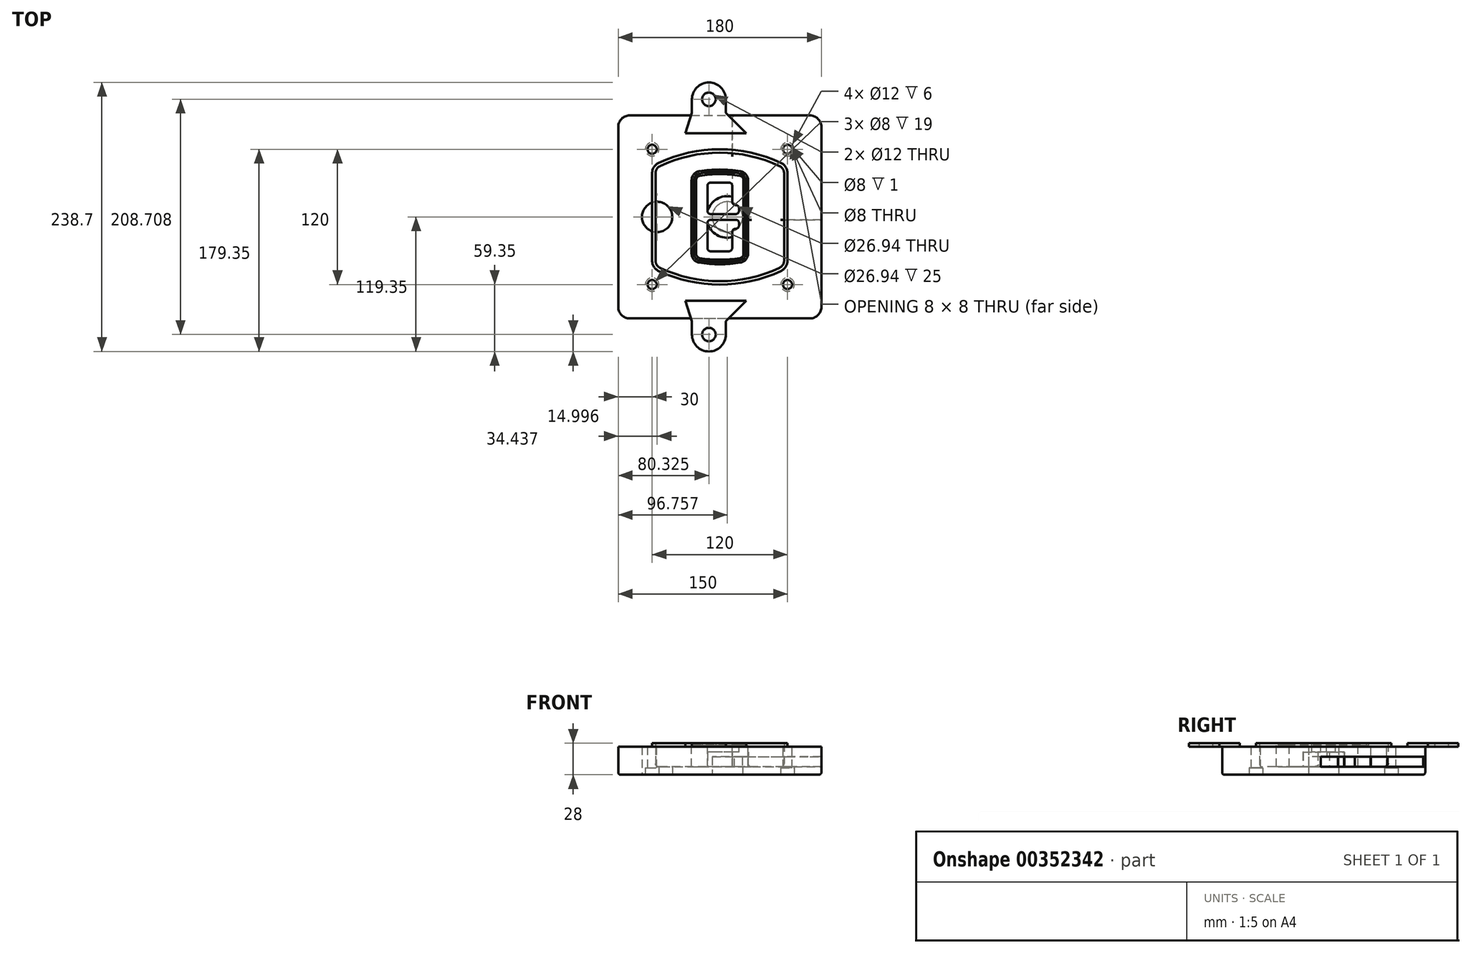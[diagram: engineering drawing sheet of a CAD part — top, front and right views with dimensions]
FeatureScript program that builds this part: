
annotation { "Feature Type Name" : "Feature", "Feature Type Description" : "" }
export const myFeature = defineFeature(function(context is Context, id is Id, definition is map)
    precondition{}
    {
        {
            var Q0;
            Q0=qCreatedBy(makeId("Top.planeOp"),FACE);
            var sketch = newSketch(context, id + "F0", { "sketchPlane" : qUnion([Q0])});
            skPoint(sketch, "E0.rect.middle", {"position": v(0, 0) * mm});
            skLineSegment(sketch, "E1.bottom", {"start": v(-80, -90) * mm, "end": v(80, -90) * mm});
            skLineSegment(sketch, "E1.top", {"start": v(-80, 90) * mm, "end": v(80, 90) * mm});
            skLineSegment(sketch, "E1.left", {"start": v(-90, -80) * mm, "end": v(-90, 80) * mm});
            skLineSegment(sketch, "E1.right", {"start": v(90, -80) * mm, "end": v(90, 80) * mm});
            skLineSegment(sketch, "E2", {"start": v(-90, 90) * mm, "end": v(90, -90) * mm, "construction": true});
            skLineSegment(sketch, "E3", {"start": v(90, 90) * mm, "end": v(-90, -90) * mm, "construction": true});
            skCircle(sketch, "E4", {"center": v(-60, 60) * mm, "radius": 4 * mm});
            skCircle(sketch, "E5", {"center": v(60, 60) * mm, "radius": 4 * mm});
            skCircle(sketch, "E6", {"center": v(60, -60) * mm, "radius": 4 * mm});
            skCircle(sketch, "E7", {"center": v(-60, -60) * mm, "radius": 4 * mm});
            skLineSegment(sketch, "E8", {"start": v(-60, 60) * mm, "end": v(60, 60) * mm, "construction": true});
            skLineSegment(sketch, "E9", {"start": v(60, 60) * mm, "end": v(60, -60) * mm, "construction": true});
            skLineSegment(sketch, "E10", {"start": v(60, -60) * mm, "end": v(-60, -60) * mm, "construction": true});
            skLineSegment(sketch, "E11", {"start": v(-60, -60) * mm, "end": v(-60, 60) * mm, "construction": true});
            skLineSegment(sketch, "E12", {"start": v(-60, 38.83) * mm, "end": v(-60, -38.83) * mm});
            skLineSegment(sketch, "E13", {"start": v(60, 38.83) * mm, "end": v(60, -38.83) * mm});
            skArc(sketch, "E14", {"start": v(54.26, 47.88) * mm, "mid": v(0, 60) * mm, "end": v(-54.26, 47.88) * mm});
            skArc(sketch, "E15", {"start": v(-54.26, -47.88) * mm, "mid": v(0, -60) * mm, "end": v(54.26, -47.88) * mm});
            skLineSegment(sketch, "E16", {"start": v(-60, 0) * mm, "end": v(60, 0) * mm, "construction": true});
            skPoint(sketch, "E17.visualSharp", {"position": v(-60, -45) * mm});
            skArc(sketch, "E17.filletArc", {"start": v(-60, -38.83) * mm, "mid": v(-58.44, -44.2) * mm, "end": v(-54.26, -47.88) * mm});
            skPoint(sketch, "E18.visualSharp", {"position": v(-60, 45) * mm});
            skArc(sketch, "E18.filletArc", {"start": v(-54.26, 47.88) * mm, "mid": v(-58.44, 44.2) * mm, "end": v(-60, 38.83) * mm});
            skPoint(sketch, "E19.visualSharp", {"position": v(60, 45) * mm});
            skArc(sketch, "E19.filletArc", {"start": v(60, 38.83) * mm, "mid": v(58.44, 44.2) * mm, "end": v(54.26, 47.88) * mm});
            skPoint(sketch, "E20.visualSharp", {"position": v(60, -45) * mm});
            skArc(sketch, "E20.filletArc", {"start": v(54.26, -47.88) * mm, "mid": v(58.44, -44.2) * mm, "end": v(60, -38.83) * mm});
            skPoint(sketch, "E21.visualSharp", {"position": v(-90, 90) * mm});
            skArc(sketch, "E21.filletArc", {"start": v(-80, 90) * mm, "mid": v(-87.07, 87.07) * mm, "end": v(-90, 80) * mm});
            skPoint(sketch, "E22.visualSharp", {"position": v(90, 90) * mm});
            skArc(sketch, "E22.filletArc", {"start": v(90, 80) * mm, "mid": v(87.07, 87.07) * mm, "end": v(80, 90) * mm});
            skPoint(sketch, "E23.visualSharp", {"position": v(90, -90) * mm});
            skArc(sketch, "E23.filletArc", {"start": v(80, -90) * mm, "mid": v(87.07, -87.07) * mm, "end": v(90, -80) * mm});
            skPoint(sketch, "E24.visualSharp", {"position": v(-90, -90) * mm});
            skArc(sketch, "E24.filletArc", {"start": v(-90, -80) * mm, "mid": v(-87.07, -87.07) * mm, "end": v(-80, -90) * mm});
            skArc(sketch, "E25.0", {"start": v(57, 38.83) * mm, "mid": v(55.9, 42.58) * mm, "end": v(52.98, 45.17) * mm});
            skLineSegment(sketch, "E25.1", {"start": v(57, 38.83) * mm, "end": v(57, -38.83) * mm});
            skArc(sketch, "E25.2", {"start": v(52.98, -45.17) * mm, "mid": v(55.9, -42.58) * mm, "end": v(57, -38.83) * mm});
            skArc(sketch, "E25.3", {"start": v(-52.98, -45.17) * mm, "mid": v(0, -57) * mm, "end": v(52.98, -45.17) * mm});
            skArc(sketch, "E25.4", {"start": v(-57, -38.83) * mm, "mid": v(-55.9, -42.58) * mm, "end": v(-52.98, -45.17) * mm});
            skArc(sketch, "E25.5", {"start": v(52.98, 45.17) * mm, "mid": v(0, 57) * mm, "end": v(-52.98, 45.17) * mm});
            skLineSegment(sketch, "E25.6", {"start": v(-57, 38.83) * mm, "end": v(-57, -38.83) * mm});
            skArc(sketch, "E25.7", {"start": v(-52.98, 45.17) * mm, "mid": v(-55.9, 42.58) * mm, "end": v(-57, 38.83) * mm});
            skArc(sketch, "E26.0", {"start": v(-55.96, 51.5) * mm, "mid": v(-61.82, 46.33) * mm, "end": v(-64, 38.83) * mm});
            skArc(sketch, "E26.1", {"start": v(55.96, 51.5) * mm, "mid": v(0, 64) * mm, "end": v(-55.96, 51.5) * mm});
            skArc(sketch, "E26.2", {"start": v(64, 38.83) * mm, "mid": v(61.82, 46.33) * mm, "end": v(55.96, 51.5) * mm});
            skLineSegment(sketch, "E26.3", {"start": v(64, 38.83) * mm, "end": v(64, -38.83) * mm});
            skArc(sketch, "E26.4", {"start": v(55.96, -51.5) * mm, "mid": v(61.82, -46.33) * mm, "end": v(64, -38.83) * mm});
            skLineSegment(sketch, "E26.5", {"start": v(-64, 38.83) * mm, "end": v(-64, -38.83) * mm});
            skArc(sketch, "E26.6", {"start": v(-55.96, -51.5) * mm, "mid": v(0, -64) * mm, "end": v(55.96, -51.5) * mm});
            skArc(sketch, "E26.7", {"start": v(-64, -38.83) * mm, "mid": v(-61.82, -46.33) * mm, "end": v(-55.96, -51.5) * mm});
            skSolve(sketch);
        }
        {
            var Q0;
            Q0=makeQuery(id+"F0.imprint","IMPRINT",FACE,{"disambiguationData":[TD([[makeQuery(id+"F0.imprint","IMPRINT",EDGE,{"derivedFrom":sQuery(id+"F0.wireOp",EDGE,"E1.bottom")}),1.0]])]});
            var Q1;
            Q1=makeQuery(id+"F0.imprint","IMPRINT",FACE,{"disambiguationData":[TD([[makeQuery(id+"F0.imprint","IMPRINT",EDGE,{"derivedFrom":sQuery(id+"F0.wireOp",EDGE,"E12")}),1.0]])]});
            var Q2;
            Q2=makeQuery(id+"F0.imprint","IMPRINT",FACE,{"disambiguationData":[TD([[makeQuery(id+"F0.imprint","IMPRINT",EDGE,{"derivedFrom":sQuery(id+"F0.wireOp",EDGE,"E25.0")}),1.0]])]});
            var Q3;
            Q3=makeQuery(id+"F0.imprint","IMPRINT",FACE,{"disambiguationData":[TD([[makeQuery(id+"F0.imprint","IMPRINT",EDGE,{"derivedFrom":sQuery(id+"F0.wireOp",EDGE,"E12")}),-1.0]])]});
            extrude(context, id + "F1", {"entities" : qUnion([Q0, Q1, Q2, Q3]), "oppositeDirection" : true, "depth" : 25 * mm});
        }
        {
            var Q0;
            Q0=makeQuery(id+"F0.imprint","IMPRINT",FACE,{"disambiguationData":[TD([[makeQuery(id+"F0.imprint","IMPRINT",EDGE,{"derivedFrom":sQuery(id+"F0.wireOp",EDGE,"E12")}),1.0]])]});
            extrude(context, id + "F2", {"entities" : qUnion([Q0]), "operationType" : NewBodyOperationType.ADD, "depth" : 3 * mm});
        }
        {
            var Q0;
            Q0=makeQuery(id+"F0.imprint","IMPRINT",FACE,{"disambiguationData":[TD([[makeQuery(id+"F0.imprint","IMPRINT",EDGE,{"derivedFrom":sQuery(id+"F0.wireOp",EDGE,"E25.0")}),1.0]])]});
            extrude(context, id + "F3", {"entities" : qUnion([Q0]), "operationType" : NewBodyOperationType.REMOVE, "oppositeDirection" : true, "depth" : 18 * mm});
        }
        {
            var Q0;
            Q0=makeQuery(id+"F2.opExtrude","CAP_FACE",FACE,{"disambiguationData":[OSD([sQuery(id+"F0.wireOp",EDGE,"E12"),sQuery(id+"F0.wireOp",EDGE,"E13"),sQuery(id+"F0.wireOp",EDGE,"E14"),sQuery(id+"F0.wireOp",EDGE,"E15"),sQuery(id+"F0.wireOp",EDGE,"E17.filletArc"),sQuery(id+"F0.wireOp",EDGE,"E18.filletArc"),sQuery(id+"F0.wireOp",EDGE,"E19.filletArc"),sQuery(id+"F0.wireOp",EDGE,"E20.filletArc"),sQuery(id+"F0.wireOp",EDGE,"E25.0"),sQuery(id+"F0.wireOp",EDGE,"E25.1"),sQuery(id+"F0.wireOp",EDGE,"E25.2"),sQuery(id+"F0.wireOp",EDGE,"E25.3"),sQuery(id+"F0.wireOp",EDGE,"E25.4"),sQuery(id+"F0.wireOp",EDGE,"E25.5"),sQuery(id+"F0.wireOp",EDGE,"E25.6"),sQuery(id+"F0.wireOp",EDGE,"E25.7")])],"isStart":false});
            var sketch = newSketch(context, id + "F4", { "sketchPlane" : qUnion([Q0])});
            skArc(sketch, "E27.0", {"start": v(-18.34, -40.45) * mm, "mid": v(0, -42) * mm, "end": v(18.34, -40.45) * mm});
            skArc(sketch, "E28.0", {"start": v(18.34, 40.45) * mm, "mid": v(0, 42) * mm, "end": v(-18.34, 40.45) * mm});
            skLineSegment(sketch, "E29", {"start": v(-25, 32.57) * mm, "end": v(-25, -32.57) * mm});
            skLineSegment(sketch, "E30", {"start": v(25, 32.57) * mm, "end": v(25, -32.57) * mm});
            skLineSegment(sketch, "E31", {"start": v(-25, 39.1) * mm, "end": v(25, 39.1) * mm, "construction": true});
            skLineSegment(sketch, "E32", {"start": v(-25, -39.1) * mm, "end": v(25, -39.1) * mm, "construction": true});
            skPoint(sketch, "E33.visualSharp", {"position": v(-25, 39.1) * mm});
            skArc(sketch, "E33.filletArc", {"start": v(-18.34, 40.45) * mm, "mid": v(-23.11, 37.73) * mm, "end": v(-25, 32.57) * mm});
            skPoint(sketch, "E34.visualSharp", {"position": v(25, 39.1) * mm});
            skArc(sketch, "E34.filletArc", {"start": v(25, 32.57) * mm, "mid": v(23.11, 37.73) * mm, "end": v(18.34, 40.45) * mm});
            skPoint(sketch, "E35.visualSharp", {"position": v(25, -39.1) * mm});
            skArc(sketch, "E35.filletArc", {"start": v(18.34, -40.45) * mm, "mid": v(23.11, -37.73) * mm, "end": v(25, -32.57) * mm});
            skPoint(sketch, "E36.visualSharp", {"position": v(-25, -39.1) * mm});
            skArc(sketch, "E36.filletArc", {"start": v(-25, -32.57) * mm, "mid": v(-23.11, -37.73) * mm, "end": v(-18.34, -40.45) * mm});
            skArc(sketch, "E37.0", {"start": v(52.98, 45.17) * mm, "mid": v(0, 57) * mm, "end": v(-52.98, 45.17) * mm});
            skArc(sketch, "E37.1", {"start": v(-52.98, 45.17) * mm, "mid": v(-55.9, 42.58) * mm, "end": v(-57, 38.83) * mm});
            skLineSegment(sketch, "E37.2", {"start": v(-57, 38.83) * mm, "end": v(-57, -38.83) * mm});
            skArc(sketch, "E37.3", {"start": v(-57, -38.83) * mm, "mid": v(-55.9, -42.58) * mm, "end": v(-52.98, -45.17) * mm});
            skArc(sketch, "E37.4", {"start": v(-52.98, -45.17) * mm, "mid": v(0, -57) * mm, "end": v(52.98, -45.17) * mm});
            skArc(sketch, "E37.5", {"start": v(52.98, -45.17) * mm, "mid": v(55.9, -42.58) * mm, "end": v(57, -38.83) * mm});
            skLineSegment(sketch, "E37.6", {"start": v(57, 38.83) * mm, "end": v(57, -38.83) * mm});
            skArc(sketch, "E37.7", {"start": v(57, 38.83) * mm, "mid": v(55.9, 42.58) * mm, "end": v(52.98, 45.17) * mm});
            skLineSegment(sketch, "E38.0", {"start": v(23, 32.57) * mm, "end": v(23, -32.57) * mm});
            skArc(sketch, "E38.1", {"start": v(18, -38.48) * mm, "mid": v(21.58, -36.44) * mm, "end": v(23, -32.57) * mm});
            skArc(sketch, "E38.2", {"start": v(-18, -38.48) * mm, "mid": v(0, -40) * mm, "end": v(18, -38.48) * mm});
            skArc(sketch, "E38.3", {"start": v(-23, -32.57) * mm, "mid": v(-21.58, -36.44) * mm, "end": v(-18, -38.48) * mm});
            skLineSegment(sketch, "E38.4", {"start": v(-23, 32.57) * mm, "end": v(-23, -32.57) * mm});
            skArc(sketch, "E38.5", {"start": v(23, 32.57) * mm, "mid": v(21.58, 36.44) * mm, "end": v(18, 38.48) * mm});
            skArc(sketch, "E38.6", {"start": v(-18, 38.48) * mm, "mid": v(-21.58, 36.44) * mm, "end": v(-23, 32.57) * mm});
            skArc(sketch, "E38.7", {"start": v(18, 38.48) * mm, "mid": v(0, 40) * mm, "end": v(-18, 38.48) * mm});
            skArc(sketch, "E39.0", {"start": v(21, 32.57) * mm, "mid": v(20.06, 35.15) * mm, "end": v(17.67, 36.5) * mm});
            skLineSegment(sketch, "E39.1", {"start": v(21, 32.57) * mm, "end": v(21, -32.57) * mm});
            skArc(sketch, "E39.2", {"start": v(17.67, -36.5) * mm, "mid": v(20.06, -35.15) * mm, "end": v(21, -32.57) * mm});
            skArc(sketch, "E39.3", {"start": v(-17.67, -36.5) * mm, "mid": v(0, -38) * mm, "end": v(17.67, -36.5) * mm});
            skArc(sketch, "E39.4", {"start": v(-21, -32.57) * mm, "mid": v(-20.06, -35.15) * mm, "end": v(-17.67, -36.5) * mm});
            skArc(sketch, "E39.5", {"start": v(17.67, 36.5) * mm, "mid": v(0, 38) * mm, "end": v(-17.67, 36.5) * mm});
            skLineSegment(sketch, "E39.6", {"start": v(-21, 32.57) * mm, "end": v(-21, -32.57) * mm});
            skArc(sketch, "E39.7", {"start": v(-17.67, 36.5) * mm, "mid": v(-20.06, 35.15) * mm, "end": v(-21, 32.57) * mm});
            skLineSegment(sketch, "E40", {"start": v(-25, 0) * mm, "end": v(25, 0) * mm, "construction": true});
            skLineSegment(sketch, "E41", {"start": v(-11, 5.5) * mm, "end": v(-11, 27.5) * mm});
            skLineSegment(sketch, "E42", {"start": v(-8, 30.5) * mm, "end": v(8, 30.5) * mm});
            skLineSegment(sketch, "E43", {"start": v(11, 27.5) * mm, "end": v(11, 13.5) * mm});
            skLineSegment(sketch, "E44", {"start": v(14, 10.5) * mm, "end": v(14, 10.5) * mm});
            skLineSegment(sketch, "E45", {"start": v(17, 7.5) * mm, "end": v(17, 5.5) * mm});
            skLineSegment(sketch, "E46", {"start": v(14, 2.5) * mm, "end": v(-8, 2.5) * mm});
            skPoint(sketch, "E47.visualSharp", {"position": v(-11, 30.5) * mm});
            skArc(sketch, "E47.filletArc", {"start": v(-8, 30.5) * mm, "mid": v(-10.12, 29.62) * mm, "end": v(-11, 27.5) * mm});
            skPoint(sketch, "E48.visualSharp", {"position": v(11, 30.5) * mm});
            skArc(sketch, "E48.filletArc", {"start": v(11, 27.5) * mm, "mid": v(10.12, 29.62) * mm, "end": v(8, 30.5) * mm});
            skPoint(sketch, "E49.visualSharp", {"position": v(11, 10.5) * mm});
            skArc(sketch, "E49.filletArc", {"start": v(11, 13.5) * mm, "mid": v(11.88, 11.38) * mm, "end": v(14, 10.5) * mm});
            skPoint(sketch, "E50.visualSharp", {"position": v(17, 10.5) * mm});
            skArc(sketch, "E50.filletArc", {"start": v(17, 7.5) * mm, "mid": v(16.12, 9.62) * mm, "end": v(14, 10.5) * mm});
            skPoint(sketch, "E51.visualSharp", {"position": v(17, 2.5) * mm});
            skArc(sketch, "E51.filletArc", {"start": v(14, 2.5) * mm, "mid": v(16.12, 3.38) * mm, "end": v(17, 5.5) * mm});
            skPoint(sketch, "E52.visualSharp", {"position": v(-11, 2.5) * mm});
            skArc(sketch, "E52.filletArc", {"start": v(-11, 5.5) * mm, "mid": v(-10.12, 3.38) * mm, "end": v(-8, 2.5) * mm});
            skLineSegment(sketch, "E53.0.MirrorCS", {"start": v(14, -2.5) * mm, "end": v(-8, -2.5) * mm});
            skArc(sketch, "E54.0.MirrorCS", {"start": v(-11, -5.5) * mm, "mid": v(-10.12, -3.38) * mm, "end": v(-8, -2.5) * mm});
            skLineSegment(sketch, "E55.0.MirrorCS", {"start": v(-11, -5.5) * mm, "end": v(-11, -27.5) * mm});
            skArc(sketch, "E56.0.MirrorCS", {"start": v(-8, -30.5) * mm, "mid": v(-10.12, -29.62) * mm, "end": v(-11, -27.5) * mm});
            skLineSegment(sketch, "E57.0.MirrorCS", {"start": v(-8, -30.5) * mm, "end": v(8, -30.5) * mm});
            skArc(sketch, "E58.0.MirrorCS", {"start": v(11, -27.5) * mm, "mid": v(10.12, -29.62) * mm, "end": v(8, -30.5) * mm});
            skLineSegment(sketch, "E59.0.MirrorCS", {"start": v(11, -27.5) * mm, "end": v(11, -13.5) * mm});
            skArc(sketch, "E60.0.MirrorCS", {"start": v(11, -13.5) * mm, "mid": v(11.88, -11.38) * mm, "end": v(14, -10.5) * mm});
            skArc(sketch, "E61.0.MirrorCS", {"start": v(17, -7.5) * mm, "mid": v(16.12, -9.62) * mm, "end": v(14, -10.5) * mm});
            skLineSegment(sketch, "E62.0.MirrorCS", {"start": v(17, -7.5) * mm, "end": v(17, -5.5) * mm});
            skArc(sketch, "E63.0.MirrorCS", {"start": v(14, -2.5) * mm, "mid": v(16.12, -3.38) * mm, "end": v(17, -5.5) * mm});
            skSolve(sketch);
        }
        {
            var Q0;
            Q0=makeQuery(id+"F4.imprint","IMPRINT",FACE,{"disambiguationData":[TD([[makeQuery(id+"F4.imprint","IMPRINT",EDGE,{"derivedFrom":sQuery(id+"F4.wireOp",EDGE,"E27.0")}),1.0]])]});
            var Q1;
            Q1=makeQuery(id+"F4.imprint","IMPRINT",FACE,{"disambiguationData":[TD([[makeQuery(id+"F4.imprint","IMPRINT",EDGE,{"derivedFrom":sQuery(id+"F4.wireOp",EDGE,"E38.0")}),-1.0]])]});
            var Q2;
            Q2=makeQuery(id+"F4.imprint","IMPRINT",FACE,{"disambiguationData":[TD([[makeQuery(id+"F4.imprint","IMPRINT",EDGE,{"derivedFrom":sQuery(id+"F4.wireOp",EDGE,"E39.0")}),1.0]])]});
            extrude(context, id + "F5", {"entities" : qUnion([Q0, Q1, Q2]), "operationType" : NewBodyOperationType.ADD, "endBound" : BoundingType.UP_TO_NEXT, "oppositeDirection" : true, "depth" : 25 * mm});
        }
        {
            var Q0;
            Q0=makeQuery(id+"F4.imprint","IMPRINT",FACE,{"disambiguationData":[TD([[makeQuery(id+"F4.imprint","IMPRINT",EDGE,{"derivedFrom":sQuery(id+"F4.wireOp",EDGE,"E38.0")}),-1.0]])]});
            extrude(context, id + "F6", {"entities" : qUnion([Q0]), "operationType" : NewBodyOperationType.REMOVE, "oppositeDirection" : true, "depth" : 2 * mm});
        }
        {
            var Q0;
            Q0=makeQuery(id+"F1.opExtrude","CAP_FACE",FACE,{"disambiguationData":[OSD([sQuery(id+"F0.wireOp",EDGE,"E1.bottom"),sQuery(id+"F0.wireOp",EDGE,"E1.top"),sQuery(id+"F0.wireOp",EDGE,"E1.left"),sQuery(id+"F0.wireOp",EDGE,"E1.right"),sQuery(id+"F0.wireOp",EDGE,"E4"),sQuery(id+"F0.wireOp",EDGE,"E5"),sQuery(id+"F0.wireOp",EDGE,"E6"),sQuery(id+"F0.wireOp",EDGE,"E7"),sQuery(id+"F0.wireOp",EDGE,"E21.filletArc"),sQuery(id+"F0.wireOp",EDGE,"E22.filletArc"),sQuery(id+"F0.wireOp",EDGE,"E23.filletArc"),sQuery(id+"F0.wireOp",EDGE,"E24.filletArc")])],"isStart":false});
            var sketch = newSketch(context, id + "F7", { "sketchPlane" : qUnion([Q0])});
            skCircle(sketch, "E64", {"center": v(6.76, 0) * mm, "radius": 13.47 * mm});
            skCircle(sketch, "E65", {"center": v(-55.56, 0) * mm, "radius": 13.47 * mm});
            skLineSegment(sketch, "E66", {"start": v(90, 0) * mm, "end": v(-90, 0) * mm});
            skCircle(sketch, "E67", {"center": v(6.76, 0) * mm, "radius": 18.47 * mm});
            skCircle(sketch, "E68", {"center": v(60, -60) * mm, "radius": 6 * mm});
            skCircle(sketch, "E69", {"center": v(-60, -60) * mm, "radius": 6 * mm});
            skCircle(sketch, "E70", {"center": v(-60, 60) * mm, "radius": 6 * mm});
            skCircle(sketch, "E71", {"center": v(60, 60) * mm, "radius": 6 * mm});
            skSolve(sketch);
        }
        {
            var Q0;
            {var subQ1=sQuery(id+"F7.wireOp",EDGE,"E66");var subQ4=sQuery(id+"F7.wireOp",EDGE,"E64");var subQ6=makeQuery(id+"F7.imprint","INTERSECT",VERTEX,{"disambiguationData":[OD(0.0)],"derivedFrom":[subQ4,subQ1]});Q0=makeQuery(id+"F7.imprint","IMPRINT",FACE,{"disambiguationData":[TD([[makeQuery(id+"F7.imprint","IMPRINT",EDGE,{"disambiguationData":[TD([[subQ6,-1.0]])],"derivedFrom":subQ4}),-1.0]])]});}
            var Q1;
            {var subQ0=sQuery(id+"F7.wireOp",EDGE,"E66");var subQ1=sQuery(id+"F7.wireOp",EDGE,"E64");var subQ3=makeQuery(id+"F7.imprint","INTERSECT",VERTEX,{"disambiguationData":[OD(0.0)],"derivedFrom":[subQ1,subQ0]});Q1=makeQuery(id+"F7.imprint","IMPRINT",FACE,{"disambiguationData":[TD([[makeQuery(id+"F7.imprint","IMPRINT",EDGE,{"disambiguationData":[TD([[subQ3,-1.0]])],"derivedFrom":subQ1}),1.0]])]});}
            var Q2;
            {var subQ0=sQuery(id+"F7.wireOp",EDGE,"E66");var subQ1=sQuery(id+"F7.wireOp",EDGE,"E64");var subQ3=makeQuery(id+"F7.imprint","INTERSECT",VERTEX,{"disambiguationData":[OD(0.0)],"derivedFrom":[subQ1,subQ0]});Q2=makeQuery(id+"F7.imprint","IMPRINT",FACE,{"disambiguationData":[TD([[makeQuery(id+"F7.imprint","IMPRINT",EDGE,{"disambiguationData":[TD([[subQ3,1.0]])],"derivedFrom":subQ1}),1.0]])]});}
            var Q3;
            {var subQ1=sQuery(id+"F7.wireOp",EDGE,"E66");var subQ4=sQuery(id+"F7.wireOp",EDGE,"E64");var subQ6=makeQuery(id+"F7.imprint","INTERSECT",VERTEX,{"disambiguationData":[OD(0.0)],"derivedFrom":[subQ4,subQ1]});Q3=makeQuery(id+"F7.imprint","IMPRINT",FACE,{"disambiguationData":[TD([[makeQuery(id+"F7.imprint","IMPRINT",EDGE,{"disambiguationData":[TD([[subQ6,1.0]])],"derivedFrom":subQ4}),-1.0]])]});}
            extrude(context, id + "F8", {"entities" : qUnion([Q0, Q1, Q2, Q3]), "operationType" : NewBodyOperationType.ADD, "oppositeDirection" : true, "depth" : 20 * mm});
        }
        {
            var Q0;
            {var subQ0=sQuery(id+"F7.wireOp",EDGE,"E66");var subQ1=sQuery(id+"F7.wireOp",EDGE,"E64");var subQ3=makeQuery(id+"F7.imprint","INTERSECT",VERTEX,{"disambiguationData":[OD(0.0)],"derivedFrom":[subQ1,subQ0]});Q0=makeQuery(id+"F7.imprint","IMPRINT",FACE,{"disambiguationData":[TD([[makeQuery(id+"F7.imprint","IMPRINT",EDGE,{"disambiguationData":[TD([[subQ3,-1.0]])],"derivedFrom":subQ1}),1.0]])]});}
            var Q1;
            {var subQ0=sQuery(id+"F7.wireOp",EDGE,"E66");var subQ1=sQuery(id+"F7.wireOp",EDGE,"E64");var subQ3=makeQuery(id+"F7.imprint","INTERSECT",VERTEX,{"disambiguationData":[OD(0.0)],"derivedFrom":[subQ1,subQ0]});Q1=makeQuery(id+"F7.imprint","IMPRINT",FACE,{"disambiguationData":[TD([[makeQuery(id+"F7.imprint","IMPRINT",EDGE,{"disambiguationData":[TD([[subQ3,1.0]])],"derivedFrom":subQ1}),1.0]])]});}
            extrude(context, id + "F9", {"entities" : qUnion([Q0, Q1]), "operationType" : NewBodyOperationType.REMOVE, "oppositeDirection" : true, "depth" : 16 * mm});
        }
        {
            var Q0;
            {var subQ0=sQuery(id+"F7.wireOp",EDGE,"E66");var subQ1=sQuery(id+"F7.wireOp",EDGE,"E65");var subQ3=makeQuery(id+"F7.imprint","INTERSECT",VERTEX,{"disambiguationData":[OD(0.0)],"derivedFrom":[subQ1,subQ0]});Q0=makeQuery(id+"F7.imprint","IMPRINT",FACE,{"disambiguationData":[TD([[makeQuery(id+"F7.imprint","IMPRINT",EDGE,{"disambiguationData":[TD([[subQ3,-1.0]])],"derivedFrom":subQ1}),1.0]])]});}
            var Q1;
            {var subQ0=sQuery(id+"F7.wireOp",EDGE,"E66");var subQ1=sQuery(id+"F7.wireOp",EDGE,"E65");var subQ3=makeQuery(id+"F7.imprint","INTERSECT",VERTEX,{"disambiguationData":[OD(0.0)],"derivedFrom":[subQ1,subQ0]});Q1=makeQuery(id+"F7.imprint","IMPRINT",FACE,{"disambiguationData":[TD([[makeQuery(id+"F7.imprint","IMPRINT",EDGE,{"disambiguationData":[TD([[subQ3,1.0]])],"derivedFrom":subQ1}),1.0]])]});}
            extrude(context, id + "F10", {"entities" : qUnion([Q0, Q1]), "operationType" : NewBodyOperationType.REMOVE, "oppositeDirection" : true, "depth" : 25 * mm});
        }
        {
            var Q0;
            Q0=makeQuery(id+"F7.imprint","IMPRINT",FACE,{"disambiguationData":[TD([[makeQuery(id+"F7.imprint","IMPRINT",EDGE,{"derivedFrom":sQuery(id+"F7.wireOp",EDGE,"E68")}),1.0]])]});
            var Q1;
            Q1=makeQuery(id+"F7.imprint","IMPRINT",FACE,{"disambiguationData":[TD([[makeQuery(id+"F7.imprint","IMPRINT",EDGE,{"derivedFrom":makeQuery(id+"F1.opExtrude","CAP_EDGE",EDGE,{"disambiguationData":[OSD([sQuery(id+"F0.wireOp",EDGE,"E5")])],"isStart":false})}),-1.0]])]});
            var Q2;
            Q2=makeQuery(id+"F7.imprint","IMPRINT",FACE,{"disambiguationData":[TD([[makeQuery(id+"F7.imprint","IMPRINT",EDGE,{"derivedFrom":sQuery(id+"F7.wireOp",EDGE,"E69")}),1.0]])]});
            var Q3;
            Q3=makeQuery(id+"F7.imprint","IMPRINT",FACE,{"disambiguationData":[TD([[makeQuery(id+"F7.imprint","IMPRINT",EDGE,{"derivedFrom":makeQuery(id+"F1.opExtrude","CAP_EDGE",EDGE,{"disambiguationData":[OSD([sQuery(id+"F0.wireOp",EDGE,"E4")])],"isStart":false})}),-1.0]])]});
            var Q4;
            Q4=makeQuery(id+"F7.imprint","IMPRINT",FACE,{"disambiguationData":[TD([[makeQuery(id+"F7.imprint","IMPRINT",EDGE,{"derivedFrom":sQuery(id+"F7.wireOp",EDGE,"E70")}),1.0]])]});
            var Q5;
            Q5=makeQuery(id+"F7.imprint","IMPRINT",FACE,{"disambiguationData":[TD([[makeQuery(id+"F7.imprint","IMPRINT",EDGE,{"derivedFrom":makeQuery(id+"F1.opExtrude","CAP_EDGE",EDGE,{"disambiguationData":[OSD([sQuery(id+"F0.wireOp",EDGE,"E7")])],"isStart":false})}),-1.0]])]});
            var Q6;
            Q6=makeQuery(id+"F7.imprint","IMPRINT",FACE,{"disambiguationData":[TD([[makeQuery(id+"F7.imprint","IMPRINT",EDGE,{"derivedFrom":sQuery(id+"F7.wireOp",EDGE,"E71")}),1.0]])]});
            var Q7;
            Q7=makeQuery(id+"F7.imprint","IMPRINT",FACE,{"disambiguationData":[TD([[makeQuery(id+"F7.imprint","IMPRINT",EDGE,{"derivedFrom":makeQuery(id+"F1.opExtrude","CAP_EDGE",EDGE,{"disambiguationData":[OSD([sQuery(id+"F0.wireOp",EDGE,"E6")])],"isStart":false})}),-1.0]])]});
            extrude(context, id + "F11", {"entities" : qUnion([Q0, Q1, Q2, Q3, Q4, Q5, Q6, Q7]), "operationType" : NewBodyOperationType.REMOVE, "oppositeDirection" : true, "depth" : 6 * mm});
        }
        {
            var Q0;
            Q0=makeQuery(id+"F9.boolean.opBoolean","COPY",FACE,{"derivedFrom":makeQuery(id+"F9.opExtrude","CAP_FACE",FACE,{"disambiguationData":[OSD([sQuery(id+"F7.wireOp",EDGE,"E64")])],"isStart":false})});
            var sketch = newSketch(context, id + "F12", { "sketchPlane" : qUnion([Q0])});
            skArc(sketch, "E72.0", {"start": v(11, -88.19) * mm, "mid": v(97.1, -83.6) * mm, "end": v(92.5, 2.5) * mm});
            skLineSegment(sketch, "E72.1", {"start": v(11, -17.97) * mm, "end": v(11, -17.97) * mm});
            skLineSegment(sketch, "E73", {"start": v(92.5, -105.13) * mm, "end": v(102.3, -105.13) * mm});
            skLineSegment(sketch, "E74.0", {"start": v(92.5, 2.5) * mm, "end": v(14, 2.5) * mm});
            skArc(sketch, "E74.1", {"start": v(14, 2.5) * mm, "mid": v(16.12, 3.38) * mm, "end": v(17, 5.5) * mm});
            skLineSegment(sketch, "E74.2", {"start": v(17, 7.5) * mm, "end": v(17, 5.5) * mm});
            skArc(sketch, "E74.3", {"start": v(17, 7.5) * mm, "mid": v(16.12, 9.62) * mm, "end": v(14, 10.5) * mm});
            skArc(sketch, "E74.4", {"start": v(11, 13.5) * mm, "mid": v(11.88, 11.38) * mm, "end": v(14, 10.5) * mm});
            skLineSegment(sketch, "E74.5", {"start": v(11, 13.5) * mm, "end": v(11, -88.19) * mm});
            skLineSegment(sketch, "E74.7", {"start": v(92.5, -2.5) * mm, "end": v(14, -2.5) * mm});
            skArc(sketch, "E74.8", {"start": v(14, -2.5) * mm, "mid": v(16.12, -3.38) * mm, "end": v(17, -5.5) * mm});
            skLineSegment(sketch, "E74.9", {"start": v(17, -7.5) * mm, "end": v(17, -5.5) * mm});
            skArc(sketch, "E74.10", {"start": v(17, -7.5) * mm, "mid": v(16.12, -9.62) * mm, "end": v(14, -10.5) * mm});
            skArc(sketch, "E74.11", {"start": v(11, -13.5) * mm, "mid": v(11.88, -11.38) * mm, "end": v(14, -10.5) * mm});
            skLineSegment(sketch, "E74.12", {"start": v(11, -17.97) * mm, "end": v(11, -13.5) * mm});
            skPoint(sketch, "E75.orphan", {"position": v(11, -27.5) * mm});
            skPoint(sketch, "E76.orphan", {"position": v(-8, -2.5) * mm});
            skPoint(sketch, "E77.orphan", {"position": v(-8, 2.5) * mm});
            skPoint(sketch, "E78.orphan", {"position": v(11, 27.5) * mm});
            skSolve(sketch);
        }
        {
            var Q0;
            {var subQ7=sQuery(id+"F12.wireOp",EDGE,"E72.0");var subQ14=sQuery(id+"F12.wireOp",EDGE,"E72.1");var subQ16=sQuery(id+"F12.wireOp",EDGE,"E74.1");var subQ18=sQuery(id+"F12.wireOp",EDGE,"E74.8");Q0=qUnion([makeQuery(id+"F12.imprint","IMPRINT",FACE,{"disambiguationData":[TD([[makeQuery(id+"F12.imprint","IMPRINT",EDGE,{"derivedFrom":subQ7}),1.0]])]}),makeQuery(id+"F12.imprint","IMPRINT",FACE,{"disambiguationData":[TD([[makeQuery(id+"F12.imprint","IMPRINT",EDGE,{"derivedFrom":subQ14}),1.0]])]}),makeQuery(id+"F12.imprint","IMPRINT",FACE,{"disambiguationData":[TD([[makeQuery(id+"F12.imprint","IMPRINT",EDGE,{"derivedFrom":subQ16}),1.0]])]}),makeQuery(id+"F12.imprint","IMPRINT",FACE,{"disambiguationData":[TD([[makeQuery(id+"F12.imprint","IMPRINT",EDGE,{"derivedFrom":subQ18}),-1.0]])]})]);}
            var Q1;
            Q1=makeQuery(id+"F5.boolean.opBoolean","SPLIT",FACE,{"disambiguationData":[TD([makeQuery(id+"F5.opExtrude","SWEPT_FACE",FACE,{"disambiguationData":[OSD([sQuery(id+"F4.wireOp",EDGE,"E41")])]})])],"derivedFrom":makeQuery(id+"F3.boolean.opBoolean","COPY",FACE,{"derivedFrom":makeQuery(id+"F3.opExtrude","CAP_FACE",FACE,{"disambiguationData":[OSD([sQuery(id+"F0.wireOp",EDGE,"E25.0"),sQuery(id+"F0.wireOp",EDGE,"E25.1"),sQuery(id+"F0.wireOp",EDGE,"E25.2"),sQuery(id+"F0.wireOp",EDGE,"E25.3"),sQuery(id+"F0.wireOp",EDGE,"E25.4"),sQuery(id+"F0.wireOp",EDGE,"E25.5"),sQuery(id+"F0.wireOp",EDGE,"E25.6"),sQuery(id+"F0.wireOp",EDGE,"E25.7")])],"isStart":false})})});
            extrude(context, id + "F13", {"entities" : qUnion([Q0]), "operationType" : NewBodyOperationType.REMOVE, "endBound" : BoundingType.UP_TO_SURFACE, "endBoundEntityFace" : qUnion([Q1]), "depth" : 25 * mm});
        }
        {
            var Q0;
            Q0=makeQuery(id+"F3.boolean.opBoolean","COPY",EDGE,{"derivedFrom":makeQuery(id+"F3.opExtrude","CAP_EDGE",EDGE,{"disambiguationData":[OSD([sQuery(id+"F0.wireOp",EDGE,"E25.6")])],"isStart":false})});
            var Q1;
            Q1=makeQuery(id+"F8.boolean.opBoolean","INTERSECT",EDGE,{"derivedFrom":[makeQuery(id+"F5.opExtrude","SWEPT_FACE",FACE,{"disambiguationData":[OSD([sQuery(id+"F4.wireOp",EDGE,"E30")])]}),makeQuery(id+"F8.opExtrude","CAP_FACE",FACE,{"disambiguationData":[OSD([sQuery(id+"F7.wireOp",EDGE,"E67")])],"isStart":false})]});
            var Q2;
            Q2=makeQuery(id+"F8.boolean.opBoolean","INTERSECT",EDGE,{"disambiguationData":[OD(1.0)],"derivedFrom":[makeQuery(id+"F5.opExtrude","SWEPT_FACE",FACE,{"disambiguationData":[OSD([sQuery(id+"F4.wireOp",EDGE,"E30")])]}),makeQuery(id+"F8.opExtrude","SWEPT_FACE",FACE,{"disambiguationData":[OSD([sQuery(id+"F7.wireOp",EDGE,"E67")])]})]});
            var Q3;
            {var subQ0=makeQuery(id+"F3.boolean.opBoolean","COPY",FACE,{"derivedFrom":makeQuery(id+"F3.opExtrude","CAP_FACE",FACE,{"disambiguationData":[OSD([sQuery(id+"F0.wireOp",EDGE,"E25.0"),sQuery(id+"F0.wireOp",EDGE,"E25.1"),sQuery(id+"F0.wireOp",EDGE,"E25.2"),sQuery(id+"F0.wireOp",EDGE,"E25.3"),sQuery(id+"F0.wireOp",EDGE,"E25.4"),sQuery(id+"F0.wireOp",EDGE,"E25.5"),sQuery(id+"F0.wireOp",EDGE,"E25.6"),sQuery(id+"F0.wireOp",EDGE,"E25.7")])],"isStart":false})});var subQ1=sQuery(id+"F4.wireOp",EDGE,"E30");Q3=makeQuery(id+"F8.boolean.opBoolean","SPLIT",EDGE,{"disambiguationData":[TD([makeQuery(id+"F5.opExtrude","SWEPT_FACE",FACE,{"disambiguationData":[OSD([sQuery(id+"F4.wireOp",EDGE,"E35.filletArc")])]})])],"derivedFrom":makeQuery(id+"F5.opExtrude","TWEAK_EDGE",EDGE,{"derivedFrom":[subQ0,makeQuery(id+"F4.imprint","IMPRINT",EDGE,{"derivedFrom":subQ1})]})});}
            var Q4;
            {var subQ0=sQuery(id+"F0.wireOp",EDGE,"E25.0");var subQ1=sQuery(id+"F0.wireOp",EDGE,"E25.1");var subQ2=sQuery(id+"F0.wireOp",EDGE,"E25.2");var subQ3=sQuery(id+"F0.wireOp",EDGE,"E25.3");var subQ4=sQuery(id+"F0.wireOp",EDGE,"E25.4");var subQ5=sQuery(id+"F0.wireOp",EDGE,"E25.5");var subQ6=sQuery(id+"F0.wireOp",EDGE,"E25.6");var subQ7=sQuery(id+"F0.wireOp",EDGE,"E25.7");Q4=makeQuery(id+"F8.boolean.opBoolean","INTERSECT",EDGE,{"derivedFrom":[makeQuery(id+"F5.boolean.opBoolean","SPLIT",FACE,{"disambiguationData":[TD([makeQuery(id+"F2.opExtrude","SWEPT_FACE",FACE,{"disambiguationData":[OSD([subQ0])]})])],"derivedFrom":makeQuery(id+"F3.boolean.opBoolean","COPY",FACE,{"derivedFrom":makeQuery(id+"F3.opExtrude","CAP_FACE",FACE,{"disambiguationData":[OSD([subQ0,subQ1,subQ2,subQ3,subQ4,subQ5,subQ6,subQ7])],"isStart":false})})}),makeQuery(id+"F8.opExtrude","SWEPT_FACE",FACE,{"disambiguationData":[OSD([sQuery(id+"F7.wireOp",EDGE,"E67")])]})]});}
            var Q5;
            Q5=makeQuery(id+"F8.boolean.opBoolean","INTERSECT",EDGE,{"disambiguationData":[OD(0.0)],"derivedFrom":[makeQuery(id+"F5.opExtrude","SWEPT_FACE",FACE,{"disambiguationData":[OSD([sQuery(id+"F4.wireOp",EDGE,"E30")])]}),makeQuery(id+"F8.opExtrude","SWEPT_FACE",FACE,{"disambiguationData":[OSD([sQuery(id+"F7.wireOp",EDGE,"E67")])]})]});
            fillet(context, id + "F14", {"entities" : qUnion([Q0, Q1, Q2, Q3, Q4, Q5]), "radius" : 3 * mm, "tangentPropagation" : true, "allowEdgeOverflow" : false});
        }
        {
            var Q0;
            Q0=makeQuery(id+"F1.opExtrude","CAP_EDGE",EDGE,{"disambiguationData":[OSD([sQuery(id+"F0.wireOp",EDGE,"E1.bottom")])],"isStart":false});
            fillet(context, id + "F15", {"entities" : qUnion([Q0]), "radius" : 2 * mm, "tangentPropagation" : true, "allowEdgeOverflow" : false});
        }
        {
            var Q0;
            Q0=qCreatedBy(makeId("Top.planeOp"),FACE);
            var sketch = newSketch(context, id + "F16", { "sketchPlane" : qUnion([Q0])});
            skLineSegment(sketch, "E79", {"start": v(-30.4, 74.35) * mm, "end": v(-24.68, 92.35) * mm});
            skLineSegment(sketch, "E80", {"start": v(-24.68, 92.35) * mm, "end": v(-24.68, 104.35) * mm});
            skLineSegment(sketch, "E81", {"start": v(-30.4, 74.35) * mm, "end": v(23.32, 74.35) * mm});
            skLineSegment(sketch, "E82", {"start": v(23.32, 74.35) * mm, "end": v(5.32, 92.35) * mm});
            skLineSegment(sketch, "E83", {"start": v(5.32, 92.35) * mm, "end": v(5.32, 104.35) * mm});
            skArc(sketch, "E84", {"start": v(5.32, 104.35) * mm, "mid": v(-9.68, 119.35) * mm, "end": v(-24.68, 104.35) * mm});
            skCircle(sketch, "E85", {"center": v(-9.68, 104.35) * mm, "radius": 6 * mm});
            skPoint(sketch, "E86.orphan", {"position": v(-3.53, 74.35) * mm});
            skLineSegment(sketch, "E87", {"start": v(-9.68, 104.35) * mm, "end": v(-9.68, 74.35) * mm});
            skLineSegment(sketch, "E88", {"start": v(-74.93, 0) * mm, "end": v(73.83, 0) * mm, "construction": true});
            skArc(sketch, "E89.MirrorCS", {"start": v(5.32, -104.35) * mm, "mid": v(-9.68, -119.35) * mm, "end": v(-24.68, -104.35) * mm});
            skLineSegment(sketch, "E90.MirrorCS", {"start": v(-24.68, -92.35) * mm, "end": v(-24.68, -104.35) * mm});
            skLineSegment(sketch, "E91.MirrorCS", {"start": v(5.32, -92.35) * mm, "end": v(5.32, -104.35) * mm});
            skLineSegment(sketch, "E92.MirrorCS", {"start": v(23.32, -74.35) * mm, "end": v(5.32, -92.35) * mm});
            skLineSegment(sketch, "E93.MirrorCS", {"start": v(-30.4, -74.35) * mm, "end": v(-24.68, -92.35) * mm});
            skLineSegment(sketch, "E94.MirrorCS", {"start": v(-30.4, -74.35) * mm, "end": v(23.32, -74.35) * mm});
            skCircle(sketch, "E95.MirrorC", {"center": v(-9.68, -104.35) * mm, "radius": 6 * mm});
            skLineSegment(sketch, "E96.MirrorCS", {"start": v(-9.68, -104.35) * mm, "end": v(-9.68, -74.35) * mm});
            skSolve(sketch);
        }
        {
            var Q0;
            Q0 = qSketchRegion(id + "F16", true);
            var Q1;
            Q1=makeQuery(id+"F2.opExtrude","CAP_FACE",FACE,{"disambiguationData":[OSD([sQuery(id+"F0.wireOp",EDGE,"E12"),sQuery(id+"F0.wireOp",EDGE,"E13"),sQuery(id+"F0.wireOp",EDGE,"E14"),sQuery(id+"F0.wireOp",EDGE,"E15"),sQuery(id+"F0.wireOp",EDGE,"E17.filletArc"),sQuery(id+"F0.wireOp",EDGE,"E18.filletArc"),sQuery(id+"F0.wireOp",EDGE,"E19.filletArc"),sQuery(id+"F0.wireOp",EDGE,"E20.filletArc"),sQuery(id+"F0.wireOp",EDGE,"E25.0"),sQuery(id+"F0.wireOp",EDGE,"E25.1"),sQuery(id+"F0.wireOp",EDGE,"E25.2"),sQuery(id+"F0.wireOp",EDGE,"E25.3"),sQuery(id+"F0.wireOp",EDGE,"E25.4"),sQuery(id+"F0.wireOp",EDGE,"E25.5"),sQuery(id+"F0.wireOp",EDGE,"E25.6"),sQuery(id+"F0.wireOp",EDGE,"E25.7")])],"isStart":false});
            extrude(context, id + "F17", {"entities" : qUnion([Q0]), "endBound" : BoundingType.UP_TO_SURFACE, "endBoundEntityFace" : qUnion([Q1]), "depth" : 25 * mm});
        }
    });
